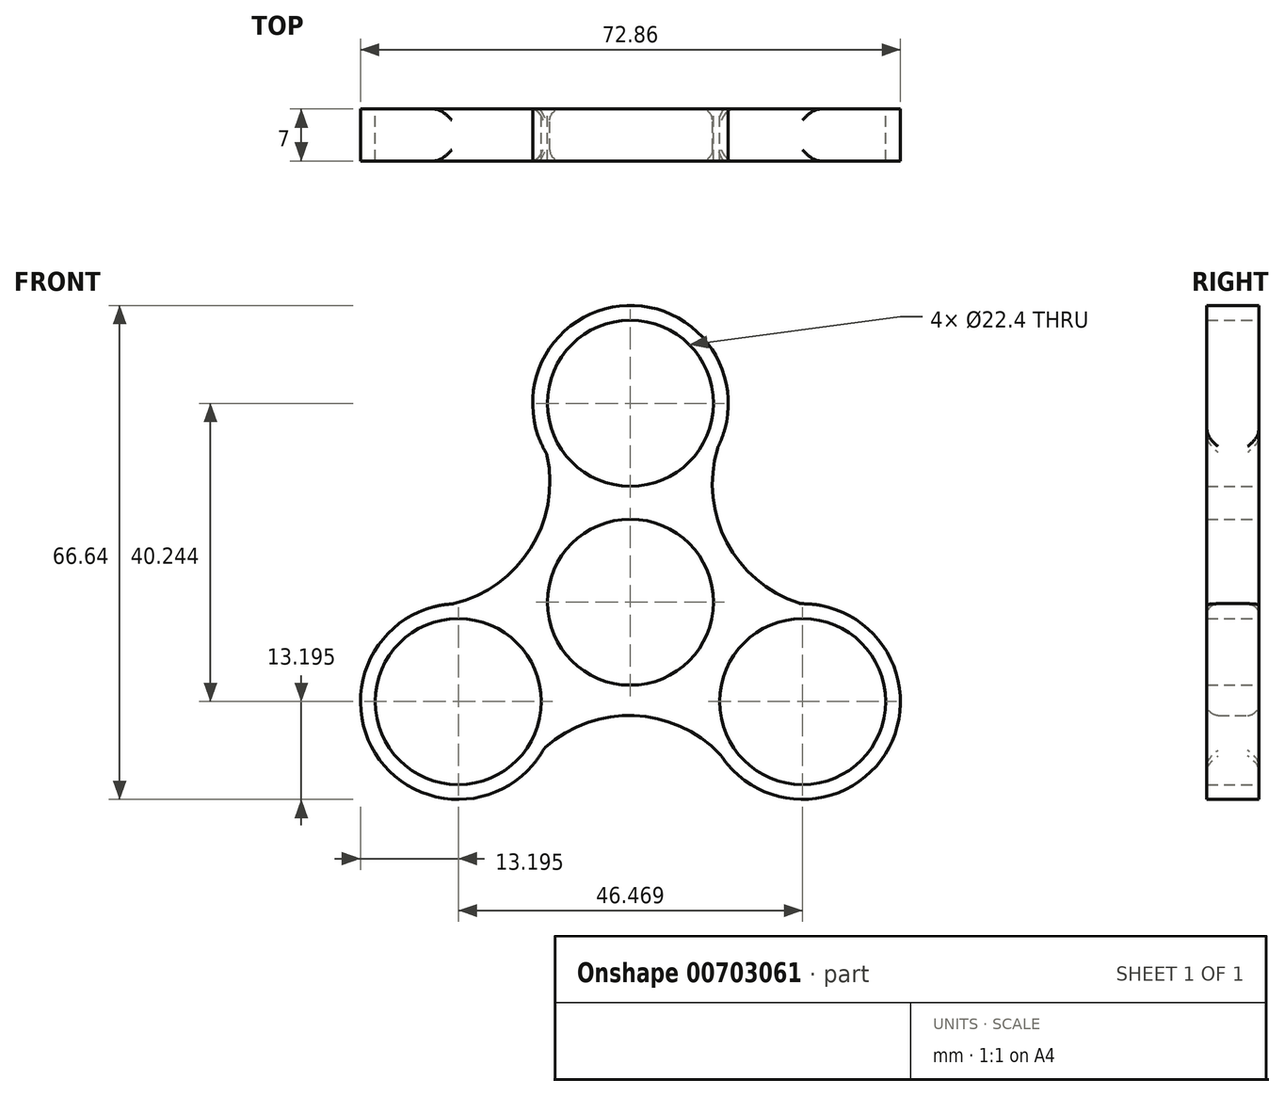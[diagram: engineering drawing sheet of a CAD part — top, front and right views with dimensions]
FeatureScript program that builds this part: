
annotation { "Feature Type Name" : "Feature", "Feature Type Description" : "" }
export const myFeature = defineFeature(function(context is Context, id is Id, definition is map)
    precondition{}
    {
        {
            var Q0;
            Q0=qCreatedBy(makeId("Front.planeOp"),FACE);
            var sketch = newSketch(context, id + "F0", { "sketchPlane" : qUnion([Q0])});
            skCircle(sketch, "E0", {"center": v(0, 0) * mm, "radius": 11.2 * mm});
            skCircle(sketch, "E1", {"center": v(0, 26.83) * mm, "radius": 11.2 * mm});
            skArc(sketch, "E2", {"start": v(11.8, 20.9) * mm, "mid": v(-0.5, 40.02) * mm, "end": v(-11.3, 20.01) * mm});
            skArc(sketch, "E3.1.0", {"start": v(-23.99, -0.24) * mm, "mid": v(-34.4, -20.45) * mm, "end": v(-11.68, -19.8) * mm});
            skArc(sketch, "E3.2.0", {"start": v(12.2, -20.66) * mm, "mid": v(34.91, -19.57) * mm, "end": v(22.98, -0.22) * mm});
            skCircle(sketch, "E4.1.0", {"center": v(-23.23, -13.41) * mm, "radius": 11.2 * mm});
            skCircle(sketch, "E4.2.0", {"center": v(23.23, -13.41) * mm, "radius": 11.2 * mm});
            skArc(sketch, "E5", {"start": v(11.8, 20.9) * mm, "mid": v(13.03, 8.03) * mm, "end": v(22.98, -0.22) * mm});
            skArc(sketch, "E6.1.0", {"start": v(-23.99, -0.24) * mm, "mid": v(-13.46, 7.27) * mm, "end": v(-11.3, 20.01) * mm});
            skArc(sketch, "E6.2.0", {"start": v(12.2, -20.66) * mm, "mid": v(0.44, -15.3) * mm, "end": v(-11.68, -19.8) * mm});
            skSolve(sketch);
        }
        {
            var Q0;
            Q0 = qSketchRegion(id + "F0", true);
            extrude(context, id + "F1", {"entities" : qUnion([Q0]), "depth" : 7 * mm, "offsetDistance" : 25 * mm});
        }
        {
            var Q0;
            Q0=makeQuery(id+"F1.opExtrude","SWEPT_FACE",FACE,{"disambiguationData":[OSD([sQuery(id+"F0.wireOp",EDGE,"E5")])]});
            var Q1;
            Q1=makeQuery(id+"F1.opExtrude","SWEPT_FACE",FACE,{"disambiguationData":[OSD([sQuery(id+"F0.wireOp",EDGE,"E6.1.0")])]});
            var Q2;
            Q2=makeQuery(id+"F1.opExtrude","SWEPT_FACE",FACE,{"disambiguationData":[OSD([sQuery(id+"F0.wireOp",EDGE,"E6.2.0")])]});
            fillet(context, id + "F2", {"entities" : qUnion([Q0, Q1, Q2]), "radius" : 1.5 * mm, "tangentPropagation" : true, "allowEdgeOverflow" : false});
        }
    });
